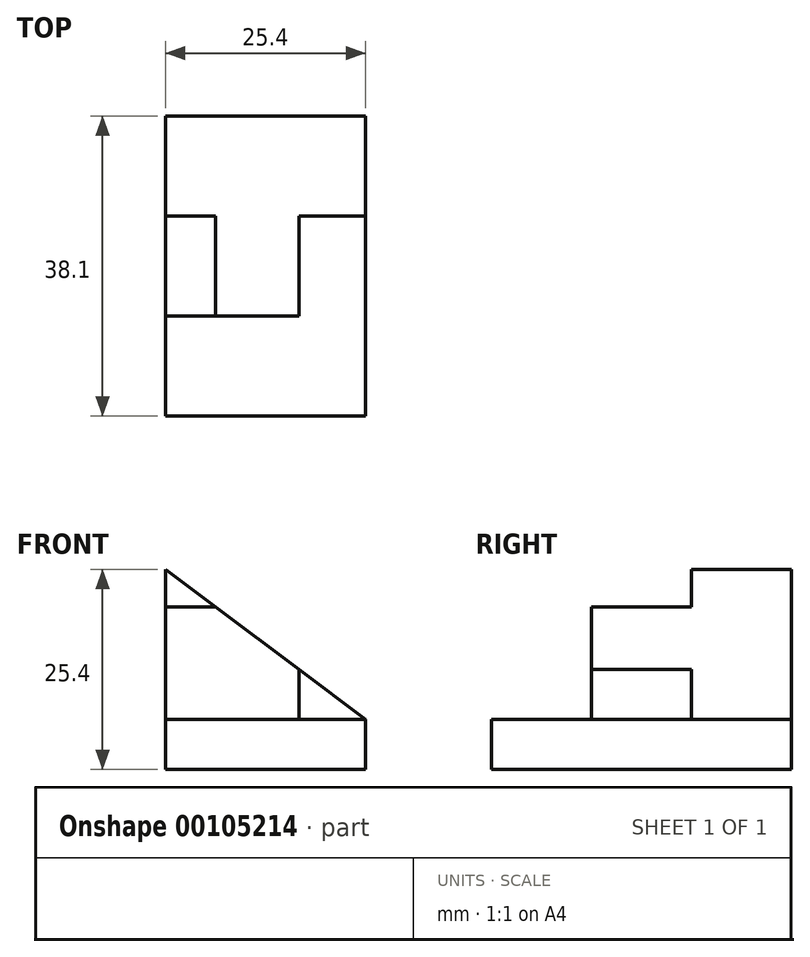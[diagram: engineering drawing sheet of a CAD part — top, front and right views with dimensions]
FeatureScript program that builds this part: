
annotation { "Feature Type Name" : "Feature", "Feature Type Description" : "" }
export const myFeature = defineFeature(function(context is Context, id is Id, definition is map)
    precondition{}
    {
        {
            var Q0;
            Q0=qCreatedBy(makeId("Front.planeOp"),FACE);
            var sketch = newSketch(context, id + "F0", { "sketchPlane" : qUnion([Q0])});
            skLineSegment(sketch, "E0", {"start": v(0, 0) * mm, "end": v(0, 6.35) * mm});
            skLineSegment(sketch, "E1", {"start": v(0, 6.35) * mm, "end": v(25.4, 6.35) * mm});
            skLineSegment(sketch, "E2", {"start": v(25.4, 6.35) * mm, "end": v(25.4, 0) * mm});
            skLineSegment(sketch, "E3", {"start": v(25.4, 0) * mm, "end": v(0, 0) * mm});
            skLineSegment(sketch, "E4", {"start": v(0, 6.35) * mm, "end": v(0, 25.4) * mm});
            skLineSegment(sketch, "E5", {"start": v(0, 25.4) * mm, "end": v(25.4, 6.35) * mm});
            skLineSegment(sketch, "E6", {"start": v(0, 20.64) * mm, "end": v(6.35, 20.64) * mm});
            skLineSegment(sketch, "E7", {"start": v(16.93, 12.7) * mm, "end": v(16.93, 6.35) * mm});
            skSolve(sketch);
        }
        {
            var Q0;
            {var subQ3=sQuery(id+"F0.wireOp",EDGE,"E0");Q0=makeQuery(id+"F0.imprint","IMPRINT",FACE,{"disambiguationData":[TD([[makeQuery(id+"F0.imprint","IMPRINT",EDGE,{"derivedFrom":subQ3}),-1.0]])]});}
            extrude(context, id + "F1", {"entities" : qUnion([Q0]), "depth" : 38.1 * mm});
        }
        {
            var Q0;
            {var subQ0=sQuery(id+"F0.wireOp",EDGE,"E6");Q0=makeQuery(id+"F0.imprint","IMPRINT",FACE,{"disambiguationData":[TD([[makeQuery(id+"F0.imprint","IMPRINT",EDGE,{"derivedFrom":subQ0}),-1.0]])]});}
            extrude(context, id + "F2", {"entities" : qUnion([Q0]), "operationType" : NewBodyOperationType.ADD, "depth" : 25.4 * mm});
        }
        {
            var Q0;
            {var subQ3=sQuery(id+"F0.wireOp",EDGE,"E6");Q0=makeQuery(id+"F0.imprint","IMPRINT",FACE,{"disambiguationData":[TD([[makeQuery(id+"F0.imprint","IMPRINT",EDGE,{"derivedFrom":subQ3}),1.0]])]});}
            extrude(context, id + "F3", {"entities" : qUnion([Q0]), "operationType" : NewBodyOperationType.ADD, "depth" : 12.7 * mm});
        }
        {
            var Q0;
            {var subQ3=sQuery(id+"F0.wireOp",EDGE,"E7");Q0=makeQuery(id+"F0.imprint","IMPRINT",FACE,{"disambiguationData":[TD([[makeQuery(id+"F0.imprint","IMPRINT",EDGE,{"derivedFrom":subQ3}),1.0]])]});}
            extrude(context, id + "F4", {"entities" : qUnion([Q0]), "operationType" : NewBodyOperationType.ADD, "depth" : 12.7 * mm});
        }
    });
